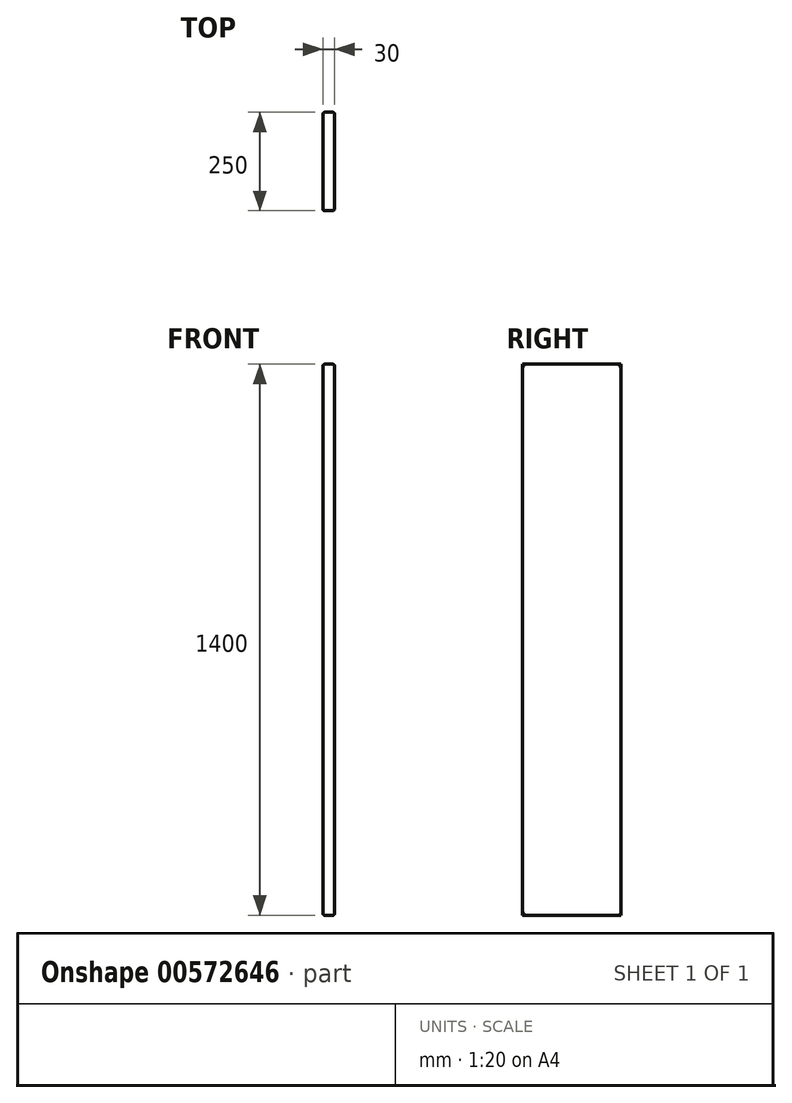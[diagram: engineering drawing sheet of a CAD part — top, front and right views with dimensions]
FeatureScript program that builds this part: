
annotation { "Feature Type Name" : "Feature", "Feature Type Description" : "" }
export const myFeature = defineFeature(function(context is Context, id is Id, definition is map)
    precondition{}
    {
        {
            var Q0;
            Q0=qCreatedBy(makeId("Top.planeOp"),FACE);
            var sketch = newSketch(context, id + "F0", { "sketchPlane" : qUnion([Q0])});
            skLineSegment(sketch, "E0.bottom", {"start": v(-13.86, 225.77) * mm, "end": v(16.14, 225.77) * mm});
            skLineSegment(sketch, "E0.top", {"start": v(-13.86, -24.23) * mm, "end": v(16.14, -24.23) * mm});
            skLineSegment(sketch, "E0.left", {"start": v(-13.86, 225.77) * mm, "end": v(-13.86, -24.23) * mm});
            skLineSegment(sketch, "E0.right", {"start": v(16.14, 225.77) * mm, "end": v(16.14, -24.23) * mm});
            skSolve(sketch);
        }
        {
            var Q0;
            Q0=makeQuery(id+"F0.imprint","IMPRINT",FACE,{"disambiguationData":[TD([[makeQuery(id+"F0.imprint","IMPRINT",EDGE,{"derivedFrom":sQuery(id+"F0.wireOp",EDGE,"E0.bottom")}),-1.0]])]});
            extrude(context, id + "F1", {"entities" : qUnion([Q0]), "depth" : 1400 * mm, "offsetDistance" : 25 * mm});
        }
        {
            var Q0;
            Q0=makeQuery(id+"F1.opExtrude","SWEPT_FACE",FACE,{"disambiguationData":[OSD([sQuery(id+"F0.wireOp",EDGE,"E0.right")])]});
            var Q1;
            Q1=makeQuery(id+"F1.opExtrude","SWEPT_FACE",FACE,{"disambiguationData":[OSD([sQuery(id+"F0.wireOp",EDGE,"E0.left")])]});
            fillet(context, id + "F2", {"entities" : qUnion([Q0, Q1]), "radius" : 5 * mm, "tangentPropagation" : true, "allowEdgeOverflow" : false});
        }
    });
